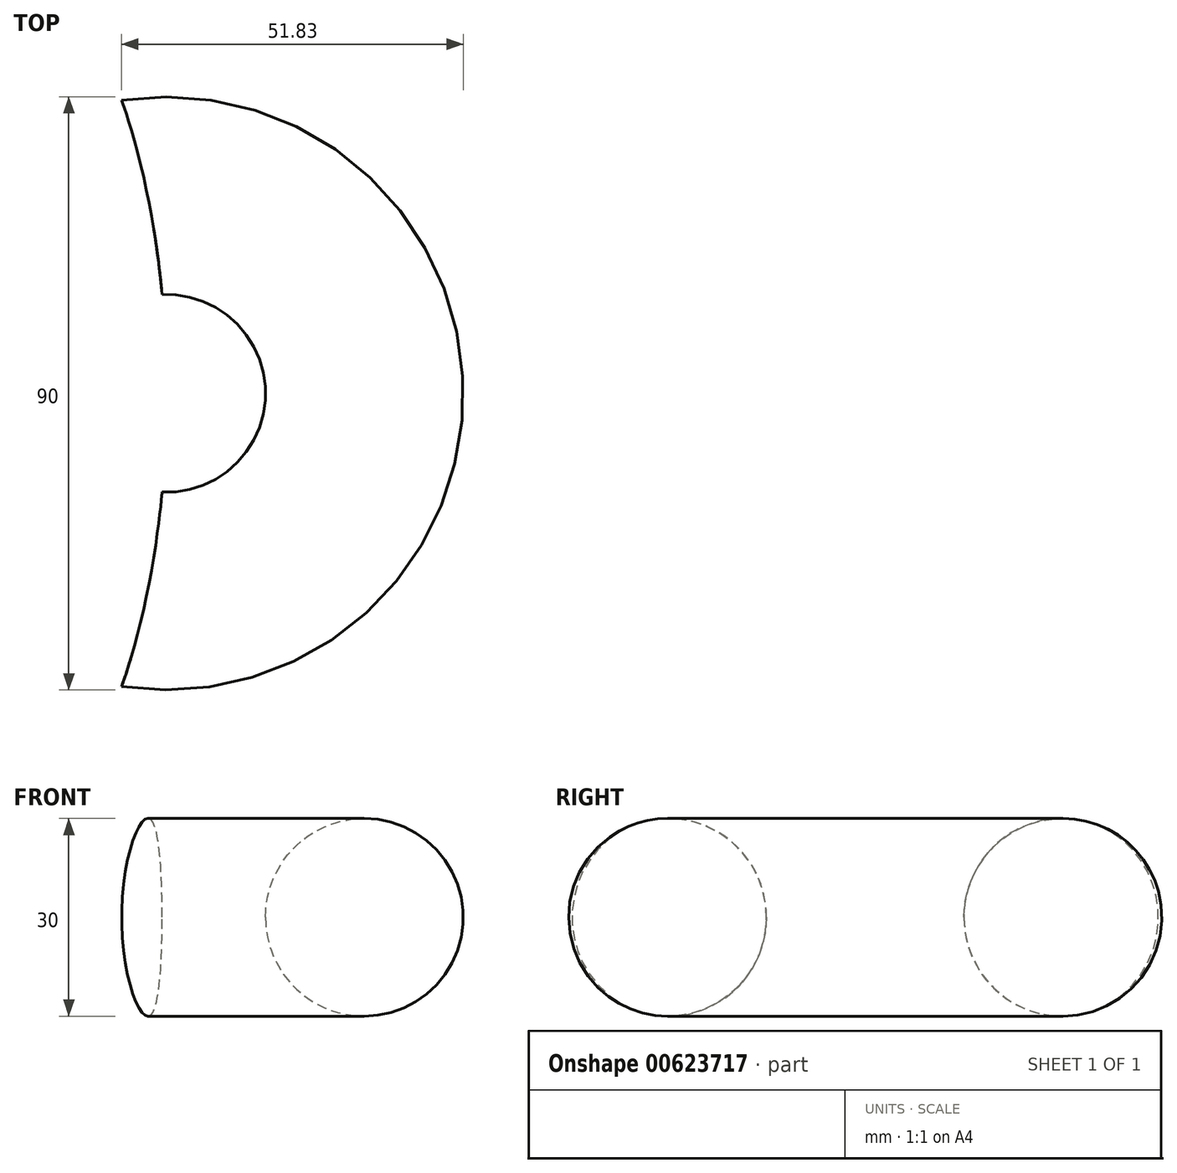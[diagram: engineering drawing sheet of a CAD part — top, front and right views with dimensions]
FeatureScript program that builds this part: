
annotation { "Feature Type Name" : "Feature", "Feature Type Description" : "" }
export const myFeature = defineFeature(function(context is Context, id is Id, definition is map)
    precondition{}
    {
        {
            var Q0;
            Q0=qCreatedBy(makeId("Front.planeOp"),FACE);
            var sketch = newSketch(context, id + "F0", { "sketchPlane" : qUnion([Q0])});
            skCircle(sketch, "E0", {"center": v(0, 0) * mm, "radius": 15 * mm});
            skLineSegment(sketch, "E1", {"start": v(30, 40.76) * mm, "end": v(30, -35.48) * mm});
            skSolve(sketch);
        }
        {
            var Q0;
            Q0=makeQuery(id+"F0.imprint","IMPRINT",FACE,{"disambiguationData":[TD([[makeQuery(id+"F0.imprint","IMPRINT",EDGE,{"derivedFrom":sQuery(id+"F0.wireOp",EDGE,"E0")}),1.0]])]});
            var Q1;
            Q1=sQuery(id+"F0.wireOp",EDGE,"E1");
            revolve(context, id + "F1", {"entities" : qUnion([Q0]), "axis" : qUnion([Q1]), "revolveType" : RevolveType.FULL});
        }
        {
            var Q0;
            Q0=qCreatedBy(makeId("Top.planeOp"),FACE);
            var sketch = newSketch(context, id + "F2", { "sketchPlane" : qUnion([Q0])});
            skEllipse(sketch, "E2", {"center": v(0, 0) * mm, "majorRadius": 70 * mm, "minorRadius": 30 * mm, "majorAxis": v(0, -1)});
            skSolve(sketch);
        }
        {
            var Q0;
            Q0 = qSketchRegion(id + "F2", true);
            extrude(context, id + "F3", {"entities" : qUnion([Q0]), "endBound" : BoundingType.SYMMETRIC, "depth" : 60 * mm, "offsetDistance" : 25 * mm});
        }
        {
            var Q0;
            Q0=makeQuery(id+"F3.opExtrude","SWEPT_FACE",FACE,{"disambiguationData":[OSD([sQuery(id+"F2.wireOp",EDGE,"E2")])]});
            var Q1;
            Q1=makeQuery(id+"F1.opRevolve","SWEPT_FACE",FACE,{"disambiguationData":[OSD([sQuery(id+"F0.wireOp",EDGE,"E0")])]});
            fillet(context, id + "F4", {"entities" : qUnion([Q0, Q1]), "radius" : 5 * mm, "tangentPropagation" : true, "allowEdgeOverflow" : false});
        }
        {
            var Q0;
            Q0=makeQuery(id+"F3.opExtrude","SWEPT_BODY",BODY,{"disambiguationData":[OSD([sQuery(id+"F2.wireOp",EDGE,"E2")])]});
            var Q1;
            Q1=makeQuery(id+"F1.opRevolve","SWEPT_BODY",BODY,{"disambiguationData":[OSD([sQuery(id+"F0.wireOp",EDGE,"E0")])]});
            booleanBodies(context, id + "F5", {"operationType" : BooleanOperationType.SUBTRACTION, "tools" : qUnion([Q0]), "targets" : qUnion([Q1])});
        }
    });
